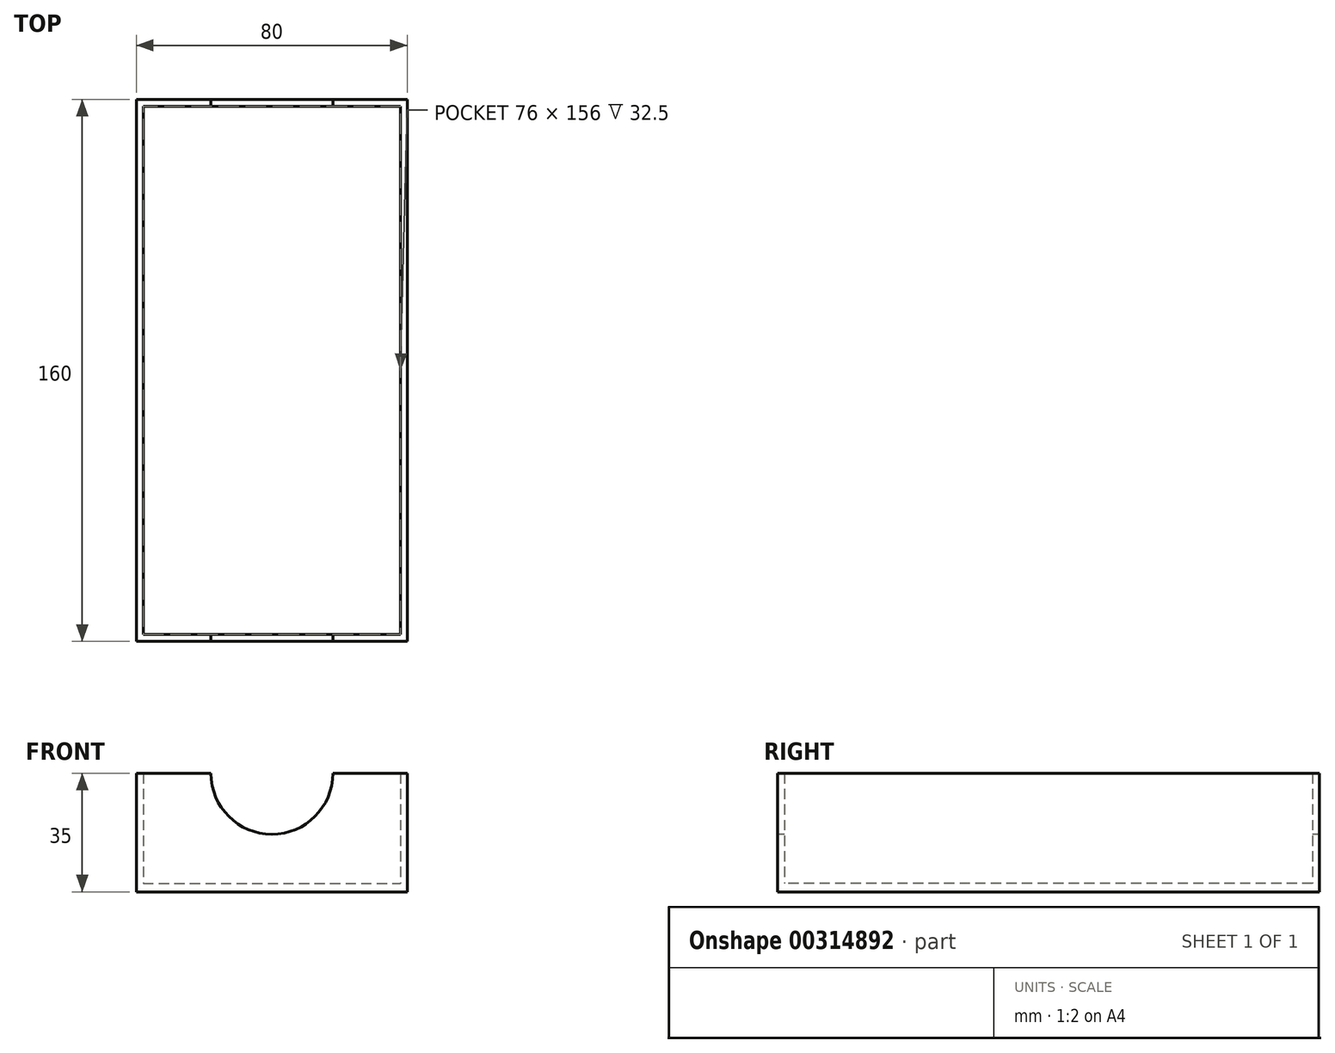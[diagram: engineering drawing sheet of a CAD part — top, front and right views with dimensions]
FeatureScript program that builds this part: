
annotation { "Feature Type Name" : "Feature", "Feature Type Description" : "" }
export const myFeature = defineFeature(function(context is Context, id is Id, definition is map)
    precondition{}
    {
        {
            var Q0;
            Q0=qCreatedBy(makeId("Top.planeOp"),FACE);
            var sketch = newSketch(context, id + "F0", { "sketchPlane" : qUnion([Q0])});
            skLineSegment(sketch, "E0.bottom", {"start": v(-102.09, -86.3) * mm, "end": v(-22.09, -86.3) * mm});
            skLineSegment(sketch, "E0.top", {"start": v(-102.09, 73.7) * mm, "end": v(-22.09, 73.7) * mm});
            skLineSegment(sketch, "E0.left", {"start": v(-102.09, -86.3) * mm, "end": v(-102.09, 73.7) * mm});
            skLineSegment(sketch, "E0.right", {"start": v(-22.09, -86.3) * mm, "end": v(-22.09, 73.7) * mm});
            skLineSegment(sketch, "E1.bottom", {"start": v(-100.09, 71.7) * mm, "end": v(-24.09, 71.7) * mm});
            skLineSegment(sketch, "E1.top", {"start": v(-100.09, -84.3) * mm, "end": v(-24.09, -84.3) * mm});
            skLineSegment(sketch, "E1.left", {"start": v(-100.09, 71.7) * mm, "end": v(-100.09, -84.3) * mm});
            skLineSegment(sketch, "E1.right", {"start": v(-24.09, 71.7) * mm, "end": v(-24.09, -84.3) * mm});
            skSolve(sketch);
        }
        {
            var Q0;
            Q0=makeQuery(id+"F0.imprint","IMPRINT",FACE,{"disambiguationData":[TD([[makeQuery(id+"F0.imprint","IMPRINT",EDGE,{"derivedFrom":sQuery(id+"F0.wireOp",EDGE,"E1.bottom")}),-1.0]])]});
            extrude(context, id + "F1", {"entities" : qUnion([Q0]), "depth" : 2.5 * mm});
        }
        {
            var Q0;
            Q0=makeQuery(id+"F0.imprint","IMPRINT",FACE,{"disambiguationData":[TD([[makeQuery(id+"F0.imprint","IMPRINT",EDGE,{"derivedFrom":sQuery(id+"F0.wireOp",EDGE,"E0.bottom")}),1.0]])]});
            extrude(context, id + "F2", {"entities" : qUnion([Q0]), "operationType" : NewBodyOperationType.ADD, "depth" : 35 * mm});
        }
        {
            var Q0;
            Q0=makeQuery(id+"F2.opExtrude","SWEPT_FACE",FACE,{"disambiguationData":[OSD([sQuery(id+"F0.wireOp",EDGE,"E0.bottom")])]});
            var sketch = newSketch(context, id + "F3", { "sketchPlane" : qUnion([Q0])});
            skCircle(sketch, "E2", {"center": v(-62.09, 35) * mm, "radius": 18 * mm});
            skSolve(sketch);
        }
        {
            var Q0;
            {var subQ0=sQuery(id+"F3.wireOp",EDGE,"E2");var subQ1=makeQuery(id+"F2.opExtrude","CAP_EDGE",EDGE,{"disambiguationData":[OSD([sQuery(id+"F0.wireOp",EDGE,"E0.bottom")])],"isStart":false});var subQ2=makeQuery(id+"F3.imprint","INTERSECT",VERTEX,{"disambiguationData":[OD(0.0)],"derivedFrom":[subQ1,subQ0]});Q0=makeQuery(id+"F3.imprint","IMPRINT",FACE,{"disambiguationData":[TD([[makeQuery(id+"F3.imprint","IMPRINT",EDGE,{"disambiguationData":[TD([[subQ2,-1.0]])],"derivedFrom":subQ0}),1.0]])]});}
            var Q1;
            Q1=sQuery(id+"F3.wireOp",EDGE,"E2");
            extrude(context, id + "F4", {"entities" : qUnion([Q0]), "operationType" : NewBodyOperationType.REMOVE, "surfaceEntities" : qUnion([Q1]), "oppositeDirection" : true, "depth" : 160 * mm});
        }
    });
